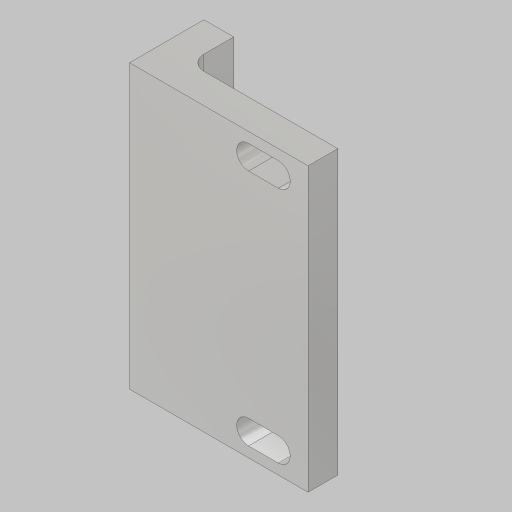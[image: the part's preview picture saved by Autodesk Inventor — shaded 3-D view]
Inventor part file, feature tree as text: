
AUTODESK INVENTOR PART (.ipt)
format: ipt  version: 2023.5 (Build 275446000, 446)  size: 140,288 bytes
history: native  units: in
note: dims shown in document units (in); Inventor stores cm internally (conversion verified against a paired STEP export)
features: sketch x3, extrude x2, hole x1, fillet x1
ambient origin geometry x8: Origin, YZ Plane, XZ Plane, XY Plane, X Axis, Y Axis, Z Axis, Center Point
bodies: Solid1 (feature_tree)
feature tree (7):
  extrude  "Extrusion1"  Depth=1.5in
  sketch  "Sketch2"  dims[d2=0.625in d3=2.375in d4=0.0in]
  hole  "Hole2"  [1 undecoded]
  extrude  "Extrusion2"  Depth=0.125in
  fillet  "Fillet2"  Radius=1.2598in
  sketch  "Sketch1"  dims[d0=0.25in d1=1.5in]
  sketch  "Sketch3"  dims[d5=2.0in d6=0.25in d14=1.2598in d15=0.104in d16=0.276in d17=0.279in d18=0.25in d19=0.5635in d20=0.75in d21=0.8108in d23=0.325in d24=0.201in d25=0.25in d26=1.0in d27=0.0in d28=0.125in]
note: 1 required parameter value undecoded (feature->parameter linkage not recoverable at this tier; creation-order binding heuristic only, values carry confidence <= 0.55)
